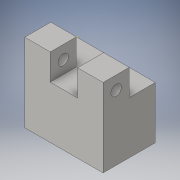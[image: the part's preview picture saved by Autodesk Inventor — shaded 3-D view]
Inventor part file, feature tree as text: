
AUTODESK INVENTOR PART (.ipt)
format: ipt  version: 2016 (Build 200138000, 138)  size: 114,176 bytes
history: native  units: in
note: dims shown in document units (in); Inventor stores cm internally (conversion verified against a paired STEP export)
features: sketch x4, extrude x3, hole x1
ambient origin geometry x8: Origin, YZ Plane, XZ Plane, XY Plane, X Axis, Y Axis, Z Axis, Center Point
bodies: Solid1 (feature_tree)
feature tree (8):
  extrude  "Extrusion1"  Depth=0.25in
  sketch  "Sketch2"  dims[d2=0.25in d3=0.0in d4=0.122in]
  extrude  "Extrusion2"  Depth=0.122in
  extrude  "Extrusion3"  Depth=0.122in
  hole  "Hole1"  [1 undecoded]
  sketch  "Sketch1"  dims[d0=0.375in d1=0.25in]
  sketch  "Sketch3"  dims[d5=0.125in d6=0.0in d7=0.122in]
  sketch  "Sketch4"  dims[d8=0.125in d9=0.0in d10=0.063in d11=0.063in d12=0.05in d13=0.75in d14=0.375in d15=0.25in d16=0.5635in d17=1.0in d18=0.8108in]
note: 1 required parameter value undecoded (feature->parameter linkage not recoverable at this tier; creation-order binding heuristic only, values carry confidence <= 0.55)
